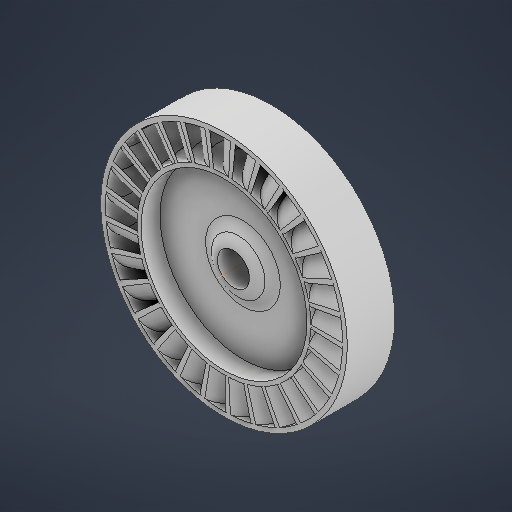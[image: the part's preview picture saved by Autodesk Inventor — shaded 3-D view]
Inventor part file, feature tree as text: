
AUTODESK INVENTOR PART (.ipt)
format: ipt  version: 2025.3 (Build 293356030, 356C)  size: 565,248 bytes
history: native  units: mm
features: sketch x5, extrude x5, sweep x1, pattern_circular x1, other x1, revolve x1
ambient origin geometry x8: Origin, YZ Plane, XZ Plane, XY Plane, X Axis, Y Axis, Z Axis, Center Point
bodies: Solid1 (feature_tree)
feature tree (14):
  sketch  "Sketch1"  dims[d0=36.6mm d1=50.0mm]
  extrude  "Extrusion1"  Depth=50.0mm
  extrude  "Extrusion2"  Depth=10.0mm TaperAngle=0.0deg
  sketch  "Sketch2"  dims[d2=2.0mm d3=0.0mm d4=10.0mm d5=0.0mm]
  sweep  "Sweep1"
  pattern_circular  "Circular Pattern1"  Count=29 Angle=360.0deg
  extrude  "Extrusion3"  Depth=10.0mm
  extrude  "Extrusion4"  Depth=10.0mm TaperAngle=0.0deg
  extrude  "Extrusion5"  Depth=10.0mm TaperAngle=0.0deg
  other  "Work Axis1"
  revolve  "Revolution1"  [1 undecoded]
  sketch  "Sketch7"  dims[d6=1.745329mm d7=0.0mm d8=0.0mm]
  sketch  "Sketch8"  dims[d10=1.0mm d11=290.0mm d12=360.0deg]
  sketch  "Sketch9"  dims[d14=35.0mm d15=52.0mm d16=10.0mm d17=0.0mm d18=10.0mm d19=0.0mm d20=6.8mm d21=0.0mm d22=0.0mm d23=90.0deg]
note: 1 required parameter value undecoded (feature->parameter linkage not recoverable at this tier; creation-order binding heuristic only, values carry confidence <= 0.55)
